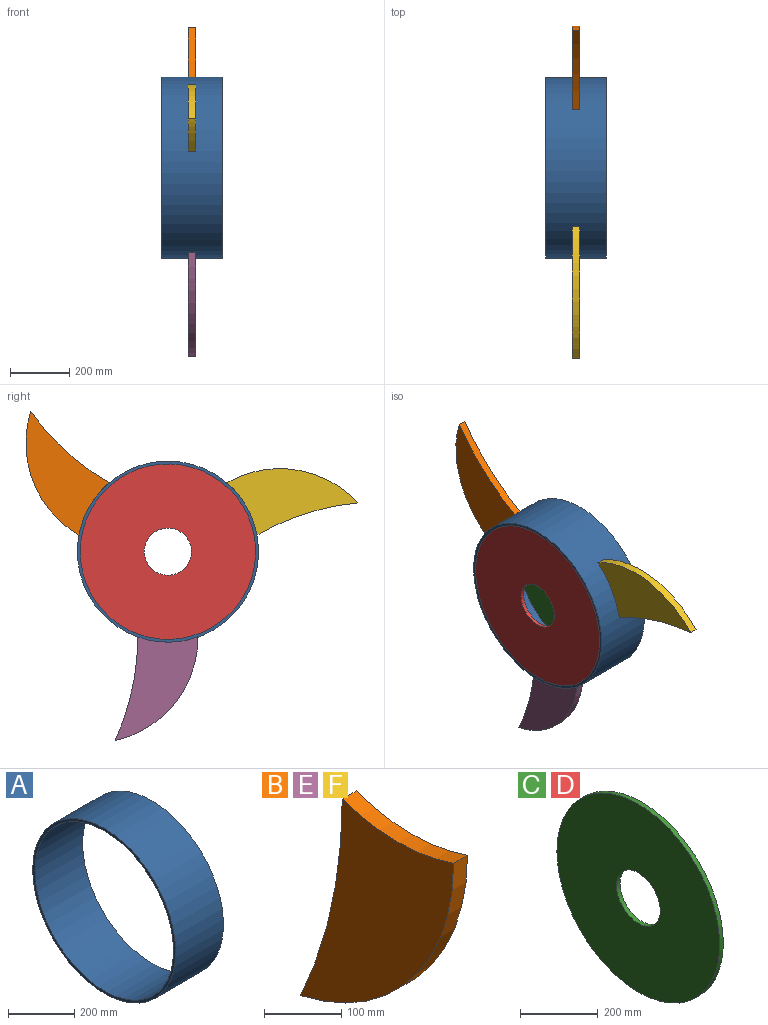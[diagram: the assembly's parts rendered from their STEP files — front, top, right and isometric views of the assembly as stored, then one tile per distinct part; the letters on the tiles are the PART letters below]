
ASSEMBLY  parts=6 mates=3
PART A: 4 faces, bbox 203.2x609.6x609.6 mm
  f0: cylinder r=295.28mm len=590.55mm, axis (-1,0,0), area 376990.4mm2, adj f2,f3
  f1: cylinder r=304.8mm len=609.6mm, axis (-1,0,0), area 389151.3mm2, adj f2,f3
  f2: plane 609.6x609.6mm, normal (1,0,0), area 17956.4mm2, adj f0,f1
  f3: plane 609.6x609.6mm, normal (-1,0,0), area 17956.4mm2, adj f0,f1
PART B: 5 faces, bbox 25.4x279.4x348.6 mm
  f0: cylinder r=304.8mm len=203.2mm, axis (-1,0,0), area 5262mm2, adj f1,f2,f3,f4
  f1: cylinder r=357.23mm len=348.65mm, axis (-1,0,0), area 12260mm2, adj f0,f2,f3,f4
  f2: cylinder r=835.7mm len=348.65mm, axis (-1,0,0), area 9135mm2, adj f0,f1,f3,f4
  f3: plane 348.65x279.4mm, normal (1,0,0), area 52390.7mm2, adj f0,f1,f2
  f4: plane 348.65x279.4mm, normal (-1,0,0), area 52390.7mm2, adj f0,f1,f2
PART C: 4 faces, bbox 12.7x590.6x590.6 mm
  f0: cylinder r=79.38mm len=158.75mm, axis (1,0,0), area 6333.8mm2, adj f2,f3
  f1: cylinder r=295.28mm len=590.55mm, axis (1,0,0), area 23561.9mm2, adj f2,f3
  f2: plane 590.55x590.55mm, normal (-1,0,0), area 254113.8mm2, adj f0,f1
  f3: plane 590.55x590.55mm, normal (1,0,0), area 254113.8mm2, adj f0,f1
PART D: same geometry as C
PART E: same geometry as B
PART F: same geometry as B
PLACE A at identity
PLACE B rot(axis=(1,0,0),120deg) t=(0,0,0)mm
PLACE C at identity
PLACE D t=(-190.5,0,0)mm
PLACE E at identity
PLACE F rot(axis=(-1,0,0),120deg) t=(0,0,0)mm
MATE fastened C.f0 <-> A.f0  axis (1,0,0) through (101.6,0,0)mm
MATE fastened D.f0 <-> A.f0  axis (-1,0,0) through (-101.6,0,0)mm
MATE fastened E.f0 <-> A.f0  axis (-1,0,0) through (0,0,0)mm
